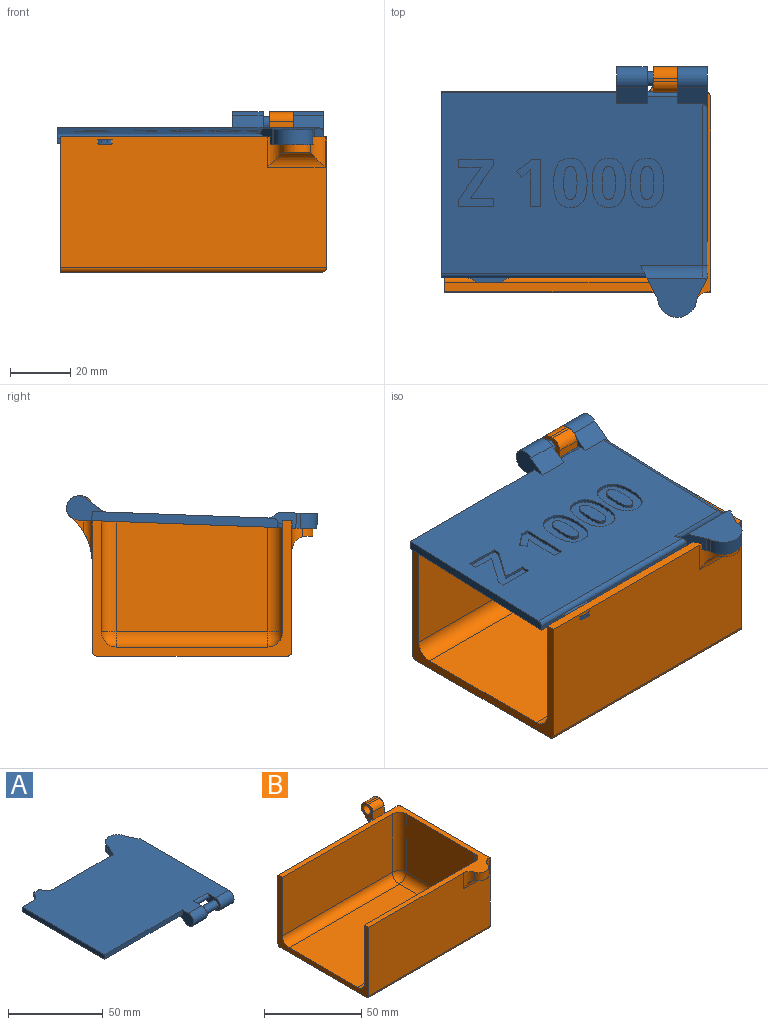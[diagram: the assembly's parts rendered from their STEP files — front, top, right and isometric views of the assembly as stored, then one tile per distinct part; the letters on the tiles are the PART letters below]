
ASSEMBLY  parts=2 mates=1
PART A: 111 faces, bbox 88x83x8.2 mm
  f0: plane 44.68x1.5mm, normal (0,1,0), area 67mm2, adj f4,f17,f25,f107
  f1: plane 7.91x1.5mm, normal (0,1,0), area 11.9mm2, adj f4,f15,f25,f106
  f2: plane 86.5x60mm, normal (0,0,-1), area 4434.7mm2, adj f3,f6,f9,f10,f11,f13,f14,f15
  f3: plane 10x7.83mm, normal (0,0.57,-0.82), area 69.5mm2, adj f2,f5,f6,f7,f23
  f4: plane 88x79mm, normal (0,0,1), area 5698.1mm2, adj f0,f1,f5,f6,f7,f9,f10,f12
  f5: cylinder r=4mm len=10mm, axis (1,0,0), area 156.2mm2, adj f3,f4,f6,f7
  f6: plane 12.42x8mm, normal (-1,0,0), area 46.1mm2, adj f2,f3,f4,f5,f8,f14
  f7: plane 70x8mm, normal (1,0,0), area 164mm2, adj f3,f4,f5,f18,f23,f24
  f8: cylinder r=2.35mm len=10mm, axis (1,0,0), area 147.7mm2, adj f6,f10
  f9: plane 58x3mm, normal (0,-1,0), area 174mm2, adj f2,f4,f13,f15
  f10: plane 12.42x8mm, normal (1,0,0), area 46.1mm2, adj f2,f4,f8,f11,f12,f14
  f11: plane 10x5.66mm, normal (0,0.57,-0.82), area 68.7mm2, adj f2,f10,f12,f13
  f12: cylinder r=4mm len=10mm, axis (1,0,0), area 156.2mm2, adj f4,f10,f11,f13
  f13: plane 12.42x8mm, normal (-1,0,0), area 62.5mm2, adj f2,f4,f9,f11,f12
  f14: cylinder r=1.5mm len=10mm, axis (1,0,0), area 47.1mm2, adj f2,f4,f6,f10
  f15: plane 61.5x3mm, normal (-1,0,0), area 184mm2, adj f1,f2,f4,f9,f25
  f16: cylinder r=6.5mm len=12.87mm, axis (0,0,1), area 92.9mm2, adj f4,f19,f21,f22
  f17: plane 10.04x5.14mm, normal (-0.89,0.46,0), area 37.2mm2, adj f0,f2,f4,f19,f20,f22,f25
  f18: plane 5.55x5mm, normal (0.88,0.47,0), area 30.9mm2, adj f4,f7,f19,f21,f24
  f19: plane 19.65x13mm, normal (0,0,-1), area 174mm2, adj f16,f17,f18,f20,f21,f22,f24
  f20: cylinder r=5mm len=20.55mm, axis (-1,0,0), area 90.2mm2, adj f2,f17,f19,f24
  f21: cylinder r=5mm len=5mm, axis (0,0,1), area 9.2mm2, adj f4,f16,f18,f19
  f22: cylinder r=5mm len=5mm, axis (0,0,1), area 7.9mm2, adj f4,f16,f17,f19
  f23: cylinder r=1.5mm len=53.58mm, axis (0,1,0), area 124.4mm2, adj f2,f3,f7,f24
  f24: torus R=6.5mm, axis (1,0,0), area 11.4mm2, adj f7,f18,f19,f20,f23
  f25: cylinder r=1.5mm len=68mm, axis (1,0,0), area 159.6mm2, adj f0,f1,f2,f15,f17,f102
  f26: extruded ~4.18x1mm, area 4.2mm2, adj f27,f41,f42,f99
  f27: extruded ~4.19x1mm, area 4.2mm2, adj f26,f28,f42,f99
  f28: extruded ~1.69x1.27mm, area 2.3mm2, adj f27,f29,f42,f99
  f29: extruded ~1.69x1.27mm, area 2.3mm2, adj f28,f30,f42,f99
  f30: extruded ~4.19x1mm, area 4.2mm2, adj f29,f31,f42,f99
  f31: extruded ~4.16x1mm, area 4.2mm2, adj f30,f32,f42,f99
  f32: extruded ~1.69x1.28mm, area 2.3mm2, adj f31,f41,f42,f99
  f33: extruded ~6.14x1.36mm, area 6.4mm2, adj f2,f34,f40,f42
  f34: extruded ~6.09x1.4mm, area 6.3mm2, adj f2,f33,f35,f42
  f35: extruded ~4.15x2.08mm, area 4.8mm2, adj f2,f34,f36,f42
  f36: extruded ~4.17x1.99mm, area 4.8mm2, adj f2,f35,f37,f42
  f37: extruded ~6.18x1.36mm, area 6.4mm2, adj f2,f36,f38,f42
  f38: extruded ~6.08x1.39mm, area 6.3mm2, adj f2,f37,f39,f42
  f39: extruded ~4.14x2.06mm, area 4.8mm2, adj f2,f38,f40,f42
  f40: extruded ~4.19x2mm, area 4.8mm2, adj f2,f33,f39,f42
  f41: extruded ~1.7x1.26mm, area 2.3mm2, adj f26,f32,f42,f99
  f42: plane 16.31x11.08mm, normal (0,0,-1), area 109.9mm2, adj f26,f27,f28,f29,f30,f31,f32,f33
  f43: extruded ~4.18x1mm, area 4.2mm2, adj f44,f58,f59,f100
  f44: extruded ~4.19x1mm, area 4.2mm2, adj f43,f45,f59,f100
  f45: extruded ~1.69x1.27mm, area 2.3mm2, adj f44,f46,f59,f100
  f46: extruded ~1.69x1.27mm, area 2.3mm2, adj f45,f47,f59,f100
  f47: extruded ~4.19x1mm, area 4.2mm2, adj f46,f48,f59,f100
  f48: extruded ~4.16x1mm, area 4.2mm2, adj f47,f49,f59,f100
  f49: extruded ~1.69x1.28mm, area 2.3mm2, adj f48,f58,f59,f100
  f50: extruded ~6.14x1.36mm, area 6.4mm2, adj f2,f51,f57,f59
  f51: extruded ~6.09x1.4mm, area 6.3mm2, adj f2,f50,f52,f59
  f52: extruded ~4.15x2.08mm, area 4.8mm2, adj f2,f51,f53,f59
  f53: extruded ~4.17x1.99mm, area 4.8mm2, adj f2,f52,f54,f59
  f54: extruded ~6.18x1.36mm, area 6.4mm2, adj f2,f53,f55,f59
  f55: extruded ~6.08x1.39mm, area 6.3mm2, adj f2,f54,f56,f59
  f56: extruded ~4.14x2.06mm, area 4.8mm2, adj f2,f55,f57,f59
  f57: extruded ~4.19x2mm, area 4.8mm2, adj f2,f50,f56,f59
  f58: extruded ~1.7x1.26mm, area 2.3mm2, adj f43,f49,f59,f100
  f59: plane 16.31x11.08mm, normal (0,0,-1), area 109.9mm2, adj f43,f44,f45,f46,f47,f48,f49,f50
  f60: plane 11.79x1mm, normal (0,-1,0), area 11.8mm2, adj f2,f61,f69,f70
  f61: plane 2.77x1mm, normal (-1,0,0), area 2.8mm2, adj f2,f60,f62,f70
  f62: plane 7.79x1mm, normal (0,1,0), area 7.8mm2, adj f2,f61,f63,f70
  f63: plane 10.9x7.59mm, normal (-0.82,-0.57,0), area 13.3mm2, adj f2,f62,f64,f70
  f64: plane 2.17x1mm, normal (-1,0,0), area 2.2mm2, adj f2,f63,f65,f70
  f65: plane 11.38x1mm, normal (0,1,0), area 11.4mm2, adj f2,f64,f66,f70
  f66: plane 2.77x1mm, normal (1,0,0), area 2.8mm2, adj f2,f65,f67,f70
  f67: plane 7.39x1mm, normal (0,-1,0), area 7.4mm2, adj f2,f66,f68,f70
  f68: plane 10.89x7.6mm, normal (0.82,0.57,0), area 13.3mm2, adj f2,f67,f69,f70
  f69: plane 2.18x1mm, normal (1,0,0), area 2.2mm2, adj f2,f60,f68,f70
  f70: plane 15.84x11.79mm, normal (0,0,-1), area 100.8mm2, adj f60,f61,f62,f63,f64,f65,f66,f67
  f71: plane 3.35x1mm, normal (0,-1,0), area 3.3mm2, adj f2,f72,f80,f81
  f72: plane 15.84x1mm, normal (-1,0,0), area 15.8mm2, adj f2,f71,f73,f81
  f73: plane 2.75x1mm, normal (0,1,0), area 2.8mm2, adj f2,f72,f74,f81
  f74: plane 5.1x4.06mm, normal (0.62,0.78,0), area 6.5mm2, adj f2,f73,f75,f81
  f75: plane 2.01x1.62mm, normal (0.78,-0.63,0), area 2.6mm2, adj f2,f74,f76,f81
  f76: plane 1.82x1.46mm, normal (-0.63,-0.78,0), area 2.3mm2, adj f2,f75,f77,f81
  f77: extruded ~1.16x1.09mm, area 1.6mm2, adj f2,f76,f78,f81
  f78: plane 1.65x1mm, normal (1,0.03,0), area 1.6mm2, adj f2,f77,f79,f81
  f79: plane 1.51x1mm, normal (1,0.02,0), area 1.5mm2, adj f2,f78,f80,f81
  f80: plane 9.17x1mm, normal (1,0,0), area 9.2mm2, adj f2,f71,f79,f81
  f81: plane 15.84x7.86mm, normal (0,0,-1), area 64.9mm2, adj f71,f72,f73,f74,f75,f76,f77,f78
  f82: extruded ~4.18x1mm, area 4.2mm2, adj f83,f97,f98,f101
  f83: extruded ~4.19x1mm, area 4.2mm2, adj f82,f84,f98,f101
  f84: extruded ~1.69x1.27mm, area 2.3mm2, adj f83,f85,f98,f101
  f85: extruded ~1.69x1.27mm, area 2.3mm2, adj f84,f86,f98,f101
  f86: extruded ~4.19x1mm, area 4.2mm2, adj f85,f87,f98,f101
  f87: extruded ~4.16x1mm, area 4.2mm2, adj f86,f88,f98,f101
  f88: extruded ~1.69x1.28mm, area 2.3mm2, adj f87,f97,f98,f101
  f89: extruded ~6.14x1.36mm, area 6.4mm2, adj f2,f90,f96,f98
  f90: extruded ~6.09x1.4mm, area 6.3mm2, adj f2,f89,f91,f98
  f91: extruded ~4.15x2.08mm, area 4.8mm2, adj f2,f90,f92,f98
  f92: extruded ~4.17x1.99mm, area 4.8mm2, adj f2,f91,f93,f98
  f93: extruded ~6.18x1.36mm, area 6.4mm2, adj f2,f92,f94,f98
  f94: extruded ~6.08x1.39mm, area 6.3mm2, adj f2,f93,f95,f98
  f95: extruded ~4.14x2.06mm, area 4.8mm2, adj f2,f94,f96,f98
  f96: extruded ~4.19x2mm, area 4.8mm2, adj f2,f89,f95,f98
  f97: extruded ~1.7x1.26mm, area 2.3mm2, adj f82,f88,f98,f101
  f98: plane 16.31x11.08mm, normal (0,0,-1), area 109.9mm2, adj f82,f83,f84,f85,f86,f87,f88,f89
  f99: plane 10.9x4.41mm, normal (0,0,-1), area 40.8mm2, adj f26,f27,f28,f29,f30,f31,f32,f41
  f100: plane 10.9x4.41mm, normal (0,0,-1), area 40.8mm2, adj f43,f44,f45,f46,f47,f48,f49,f58
  f101: plane 10.9x4.41mm, normal (0,0,-1), area 40.8mm2, adj f82,f83,f84,f85,f86,f87,f88,f97
  f102: plane 15.42x5mm, normal (0,0,-1), area 36.8mm2, adj f25,f103,f104,f105,f106,f107
  f103: plane 2x1.5mm, normal (0,1,0), area 3mm2, adj f4,f102,f104,f105
  f104: cylinder r=2mm len=1.92mm, axis (0,0,-1), area 3.8mm2, adj f4,f102,f103,f106
  f105: cylinder r=2mm len=1.92mm, axis (0,0,1), area 3.8mm2, adj f4,f102,f103,f107
  f106: cylinder r=5mm len=4.79mm, axis (0,0,-1), area 9.6mm2, adj f1,f4,f102,f104
  f107: cylinder r=5mm len=4.79mm, axis (0,0,1), area 9.6mm2, adj f0,f4,f102,f105
  f108: plane 8x8mm, normal (0,0,-1), area 50.3mm2, adj f110
  f109: plane 8x8mm, normal (0,0,1), area 50.3mm2, adj f110
  f110: cylinder r=4mm len=8mm, axis (0,0,1), area 88mm2, adj f108,f109
PART B: 41 faces, bbox 88x81.5x53 mm
  f0: plane 64.5x43.2mm, normal (1,0,0), area 2786.4mm2, adj f1,f18,f21,f29
  f1: plane 88x43.2mm, normal (0,-1,0), area 3610.8mm2, adj f0,f16,f22,f29,f34,f35,f36
  f2: plane 86.5x43.2mm, normal (0,1,0), area 3540.5mm2, adj f14,f16,f18,f19,f29,f30,f31
  f3: plane 80x36.7mm, normal (0,1,0), area 2936mm2, adj f6,f16,f23,f29
  f4: plane 50x36.7mm, normal (-1,0,0), area 1835mm2, adj f6,f7,f25,f29
  f5: plane 80x36.7mm, normal (0,-1,0), area 2936mm2, adj f7,f16,f27,f29
  f6: cylinder r=5mm len=36.7mm, axis (0,0,-1), area 288.2mm2, adj f3,f4,f24,f29
  f7: cylinder r=5mm len=36.7mm, axis (0,0,1), area 288.2mm2, adj f4,f5,f26,f29
  f8: plane 8x1.01mm, normal (0,0,1), area 8mm2, adj f10,f12,f13,f17
  f9: plane 86.5x63mm, normal (0,0,-1), area 5449.5mm2, adj f16,f19,f21,f22
  f10: cylinder r=4mm len=8mm, axis (1,0,0), area 78.1mm2, adj f8,f12,f13,f14
  f11: cylinder r=2.65mm len=8mm, axis (1,0,0), area 133.2mm2, adj f12,f13
  f12: plane 11.79x8.5mm, normal (-1,0,0), area 42.9mm2, adj f8,f10,f11,f14,f17,f28,f29,f31
  f13: plane 11.79x8.5mm, normal (1,0,0), area 42.9mm2, adj f8,f10,f11,f14,f17,f28,f29,f30
  f14: cylinder r=20mm len=15.27mm, axis (1,0,0), area 164.8mm2, adj f2,f10,f12,f13,f30,f31
  f15: plane 80x50mm, normal (0,0,1), area 4000mm2, adj f16,f23,f25,f27
  f16: plane 66x44.7mm, normal (-1,0,0), area 458mm2, adj f1,f2,f3,f5,f9,f15,f19,f22
  f17: cylinder r=3.5mm len=8mm, axis (-1,0,0), area 42.4mm2, adj f8,f12,f13,f28
  f18: cylinder r=1.5mm len=43.2mm, axis (0,0,-1), area 101.8mm2, adj f0,f2,f20,f29
  f19: cylinder r=1.5mm len=86.5mm, axis (-1,0,0), area 203.8mm2, adj f2,f9,f16,f20
  f20: sphere r=1.5mm, area 3.5mm2, adj f18,f19,f21
  f21: cylinder r=1.5mm len=64.5mm, axis (0,1,0), area 150.7mm2, adj f0,f9,f20,f22
  f22: cylinder r=1.5mm len=88mm, axis (1,0,0), area 206.1mm2, adj f1,f9,f16,f21
  f23: cylinder r=5mm len=80mm, axis (1,0,0), area 628.3mm2, adj f3,f15,f16,f24
  f24: sphere r=5mm, area 39.3mm2, adj f6,f23,f25
  f25: cylinder r=5mm len=50mm, axis (0,1,0), area 392.7mm2, adj f4,f15,f24,f26
  f26: sphere r=5mm, area 39.3mm2, adj f7,f25,f27
  f27: cylinder r=5mm len=80mm, axis (-1,0,0), area 628.3mm2, adj f5,f15,f16,f26
  f28: plane 8x5mm, normal (0,-1,0), area 40mm2, adj f12,f13,f17,f29
  f29: plane 88x76mm, normal (0,0,1), area 788.9mm2, adj f0,f1,f2,f3,f4,f5,f6,f7
  f30: cylinder r=3mm len=14.02mm, axis (0,0,-1), area 39.4mm2, adj f2,f13,f14,f29
  f31: cylinder r=3mm len=14.02mm, axis (0,0,1), area 39.4mm2, adj f2,f12,f14,f29
  f32: cylinder r=5mm len=9.54mm, axis (0,0,1), area 63.6mm2, adj f29,f33,f34,f35,f36
  f33: plane 8x2mm, normal (0,0,-1), area 11.2mm2, adj f32,f35
  f34: cylinder r=5mm len=10mm, axis (0,0,1), area 45.8mm2, adj f1,f29,f32,f35
  f35: cylinder r=5mm len=19.08mm, axis (1,0,0), area 99.3mm2, adj f1,f32,f33,f34,f36
  f36: cylinder r=5mm len=10mm, axis (0,0,1), area 45.8mm2, adj f1,f29,f32,f35
  f37: plane 8.2x6.1mm, normal (0,0,1), area 42.1mm2, adj f38,f39
  f38: cylinder r=4.1mm len=8.2mm, axis (0,0,1), area 59.7mm2, adj f37,f39,f40
  f39: plane 7.16x3.5mm, normal (0,-1,0), area 25.1mm2, adj f37,f38,f40
  f40: plane 8.2x6.1mm, normal (0,0,-1), area 42.1mm2, adj f38,f39
PLACE A rot(axis=(-1,0,0),177.9deg) t=(-44.25,73.15,99.36)mm
PLACE B t=(-43.25,0,0)mm fixed
MATE cylindrical B.f10 <-> A.f5  axis (1,0,0) through (33.75,37.5,49)mm
